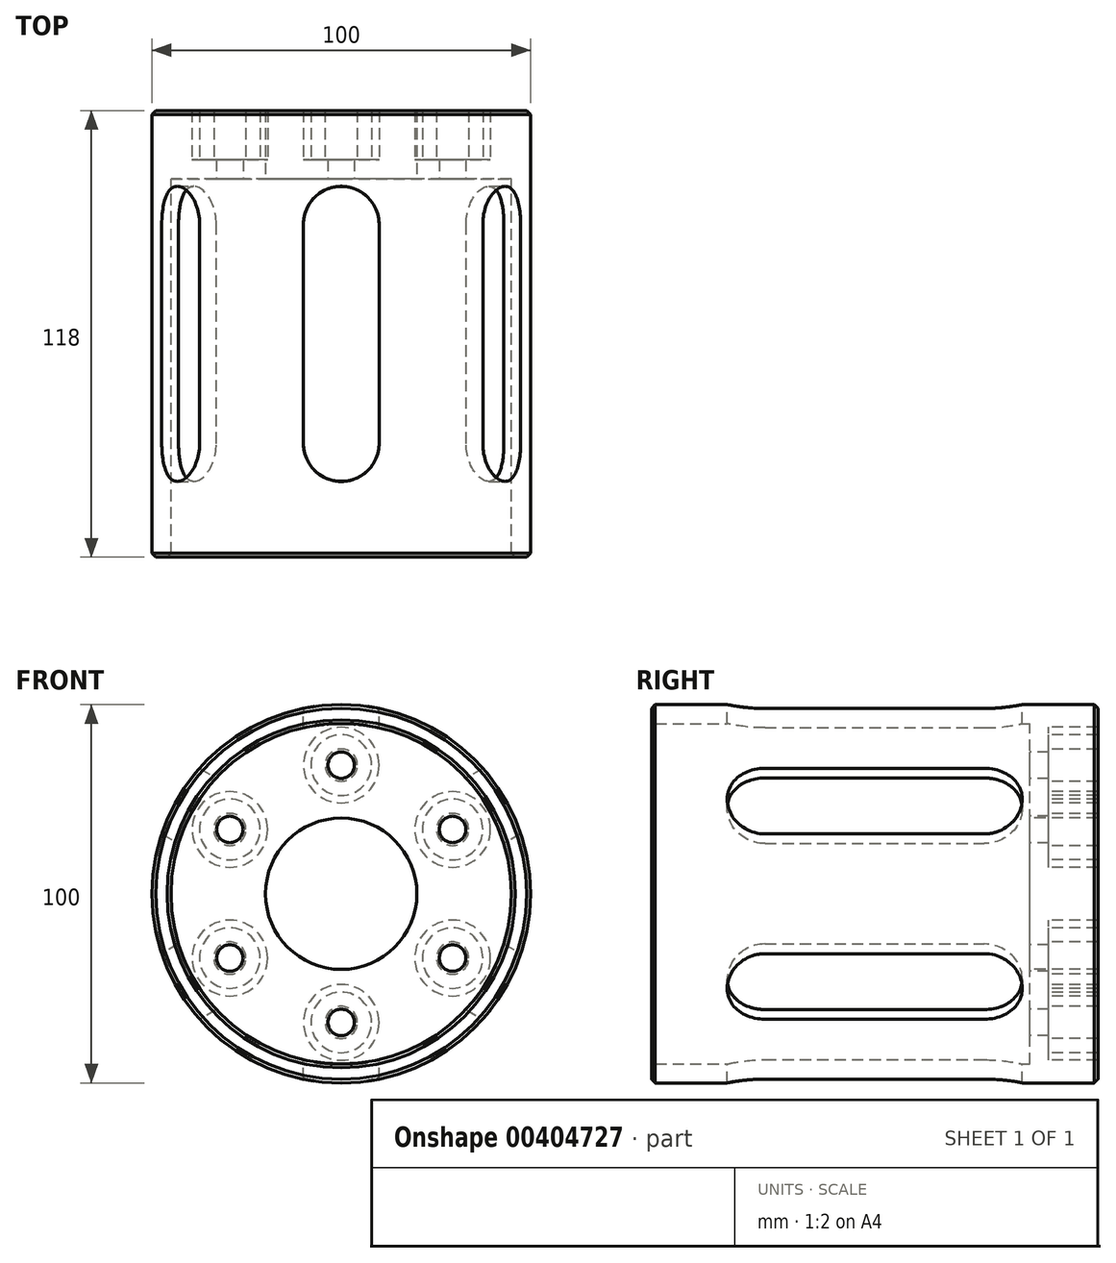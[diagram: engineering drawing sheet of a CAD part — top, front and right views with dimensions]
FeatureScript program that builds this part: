
annotation { "Feature Type Name" : "Feature", "Feature Type Description" : "" }
export const myFeature = defineFeature(function(context is Context, id is Id, definition is map)
    precondition{}
    {
        {
            var Q0;
            Q0=qCreatedBy(makeId("Top.planeOp"),FACE);
            var sketch = newSketch(context, id + "F0", { "sketchPlane" : qUnion([Q0])});
            skLineSegment(sketch, "E0", {"start": v(0, 60.4) * mm, "end": v(0, -60.4) * mm, "construction": true});
            skSolve(sketch);
        }
        {
            var Q0;
            Q0=qCreatedBy(makeId("Front.planeOp"),FACE);
            var sketch = newSketch(context, id + "F1", { "sketchPlane" : qUnion([Q0])});
            skCircle(sketch, "E1", {"center": v(0, 0) * mm, "radius": 50 * mm});
            skCircle(sketch, "E2", {"center": v(0, 34) * mm, "radius": 10 * mm});
            skCircle(sketch, "E3", {"center": v(0, 34) * mm, "radius": 4.25 * mm});
            skCircle(sketch, "E4", {"center": v(0, 34) * mm, "radius": 8 * mm});
            skCircle(sketch, "E5", {"center": v(0, 0) * mm, "radius": 20 * mm});
            skCircle(sketch, "E6", {"center": v(0, 0) * mm, "radius": 45 * mm});
            skCircle(sketch, "E7", {"center": v(0, 34) * mm, "radius": 3.5 * mm});
            skCircle(sketch, "E8.1.0", {"center": v(-29.44, 17) * mm, "radius": 3.5 * mm});
            skCircle(sketch, "E8.1.1", {"center": v(-29.44, 17) * mm, "radius": 4.25 * mm});
            skCircle(sketch, "E8.1.2", {"center": v(-29.44, 17) * mm, "radius": 10 * mm});
            skCircle(sketch, "E8.1.3", {"center": v(-29.44, 17) * mm, "radius": 8 * mm});
            skCircle(sketch, "E8.2.0", {"center": v(-29.44, -17) * mm, "radius": 3.5 * mm});
            skCircle(sketch, "E8.2.1", {"center": v(-29.44, -17) * mm, "radius": 4.25 * mm});
            skCircle(sketch, "E8.2.2", {"center": v(-29.44, -17) * mm, "radius": 10 * mm});
            skCircle(sketch, "E8.2.3", {"center": v(-29.44, -17) * mm, "radius": 8 * mm});
            skCircle(sketch, "E8.3.0", {"center": v(0, -34) * mm, "radius": 3.5 * mm});
            skCircle(sketch, "E8.3.1", {"center": v(0, -34) * mm, "radius": 4.25 * mm});
            skCircle(sketch, "E8.3.2", {"center": v(0, -34) * mm, "radius": 10 * mm});
            skCircle(sketch, "E8.3.3", {"center": v(0, -34) * mm, "radius": 8 * mm});
            skCircle(sketch, "E8.4.0", {"center": v(29.44, -17) * mm, "radius": 3.5 * mm});
            skCircle(sketch, "E8.4.1", {"center": v(29.44, -17) * mm, "radius": 4.25 * mm});
            skCircle(sketch, "E8.4.2", {"center": v(29.44, -17) * mm, "radius": 10 * mm});
            skCircle(sketch, "E8.4.3", {"center": v(29.44, -17) * mm, "radius": 8 * mm});
            skCircle(sketch, "E8.5.0", {"center": v(29.44, 17) * mm, "radius": 3.5 * mm});
            skCircle(sketch, "E8.5.1", {"center": v(29.44, 17) * mm, "radius": 4.25 * mm});
            skCircle(sketch, "E8.5.2", {"center": v(29.44, 17) * mm, "radius": 10 * mm});
            skCircle(sketch, "E8.5.3", {"center": v(29.44, 17) * mm, "radius": 8 * mm});
            skSolve(sketch);
        }
        {
            var Q0;
            Q0=makeQuery(id+"F1.imprint","IMPRINT",FACE,{"disambiguationData":[TD([[makeQuery(id+"F1.imprint","IMPRINT",EDGE,{"derivedFrom":sQuery(id+"F1.wireOp",EDGE,"E2")}),-1.0]])]});
            var Q1;
            Q1=makeQuery(id+"F1.imprint","IMPRINT",FACE,{"disambiguationData":[TD([[makeQuery(id+"F1.imprint","IMPRINT",EDGE,{"derivedFrom":sQuery(id+"F1.wireOp",EDGE,"E8.1.1")}),-1.0]])]});
            var Q2;
            Q2=makeQuery(id+"F1.imprint","IMPRINT",FACE,{"disambiguationData":[TD([[makeQuery(id+"F1.imprint","IMPRINT",EDGE,{"derivedFrom":sQuery(id+"F1.wireOp",EDGE,"E3")}),-1.0]])]});
            var Q3;
            Q3=makeQuery(id+"F1.imprint","IMPRINT",FACE,{"disambiguationData":[TD([[makeQuery(id+"F1.imprint","IMPRINT",EDGE,{"derivedFrom":sQuery(id+"F1.wireOp",EDGE,"E8.5.1")}),-1.0]])]});
            var Q4;
            Q4=makeQuery(id+"F1.imprint","IMPRINT",FACE,{"disambiguationData":[TD([[makeQuery(id+"F1.imprint","IMPRINT",EDGE,{"derivedFrom":sQuery(id+"F1.wireOp",EDGE,"E8.2.1")}),-1.0]])]});
            var Q5;
            Q5=makeQuery(id+"F1.imprint","IMPRINT",FACE,{"disambiguationData":[TD([[makeQuery(id+"F1.imprint","IMPRINT",EDGE,{"derivedFrom":sQuery(id+"F1.wireOp",EDGE,"E8.3.1")}),-1.0]])]});
            var Q6;
            Q6=makeQuery(id+"F1.imprint","IMPRINT",FACE,{"disambiguationData":[TD([[makeQuery(id+"F1.imprint","IMPRINT",EDGE,{"derivedFrom":sQuery(id+"F1.wireOp",EDGE,"E8.4.1")}),-1.0]])]});
            var Q7;
            Q7=makeQuery(id+"F1.imprint","IMPRINT",FACE,{"disambiguationData":[TD([[makeQuery(id+"F1.imprint","IMPRINT",EDGE,{"derivedFrom":sQuery(id+"F1.wireOp",EDGE,"E1")}),1.0]])]});
            extrude(context, id + "F2", {"entities" : qUnion([Q0, Q1, Q2, Q3, Q4, Q5, Q6, Q7]), "oppositeDirection" : true, "depth" : 18 * mm});
        }
        {
            var Q0;
            Q0=makeQuery(id+"F1.imprint","IMPRINT",FACE,{"disambiguationData":[TD([[makeQuery(id+"F1.imprint","IMPRINT",EDGE,{"derivedFrom":sQuery(id+"F1.wireOp",EDGE,"E2")}),1.0]])]});
            var Q1;
            Q1=makeQuery(id+"F1.imprint","IMPRINT",FACE,{"disambiguationData":[TD([[makeQuery(id+"F1.imprint","IMPRINT",EDGE,{"derivedFrom":sQuery(id+"F1.wireOp",EDGE,"E8.1.2")}),1.0]])]});
            var Q2;
            Q2=makeQuery(id+"F1.imprint","IMPRINT",FACE,{"disambiguationData":[TD([[makeQuery(id+"F1.imprint","IMPRINT",EDGE,{"derivedFrom":sQuery(id+"F1.wireOp",EDGE,"E8.2.2")}),1.0]])]});
            var Q3;
            Q3=makeQuery(id+"F1.imprint","IMPRINT",FACE,{"disambiguationData":[TD([[makeQuery(id+"F1.imprint","IMPRINT",EDGE,{"derivedFrom":sQuery(id+"F1.wireOp",EDGE,"E8.3.2")}),1.0]])]});
            var Q4;
            Q4=makeQuery(id+"F1.imprint","IMPRINT",FACE,{"disambiguationData":[TD([[makeQuery(id+"F1.imprint","IMPRINT",EDGE,{"derivedFrom":sQuery(id+"F1.wireOp",EDGE,"E8.4.2")}),1.0]])]});
            var Q5;
            Q5=makeQuery(id+"F1.imprint","IMPRINT",FACE,{"disambiguationData":[TD([[makeQuery(id+"F1.imprint","IMPRINT",EDGE,{"derivedFrom":sQuery(id+"F1.wireOp",EDGE,"E8.5.2")}),1.0]])]});
            var Q6;
            Q6=makeQuery(id+"F1.imprint","IMPRINT",FACE,{"disambiguationData":[TD([[makeQuery(id+"F1.imprint","IMPRINT",EDGE,{"derivedFrom":sQuery(id+"F1.wireOp",EDGE,"E8.1.0")}),-1.0]])]});
            var Q7;
            Q7=makeQuery(id+"F1.imprint","IMPRINT",FACE,{"disambiguationData":[TD([[makeQuery(id+"F1.imprint","IMPRINT",EDGE,{"derivedFrom":sQuery(id+"F1.wireOp",EDGE,"E3")}),1.0]])]});
            var Q8;
            Q8=makeQuery(id+"F1.imprint","IMPRINT",FACE,{"disambiguationData":[TD([[makeQuery(id+"F1.imprint","IMPRINT",EDGE,{"derivedFrom":sQuery(id+"F1.wireOp",EDGE,"E8.5.0")}),-1.0]])]});
            var Q9;
            Q9=makeQuery(id+"F1.imprint","IMPRINT",FACE,{"disambiguationData":[TD([[makeQuery(id+"F1.imprint","IMPRINT",EDGE,{"derivedFrom":sQuery(id+"F1.wireOp",EDGE,"E8.2.0")}),-1.0]])]});
            var Q10;
            Q10=makeQuery(id+"F1.imprint","IMPRINT",FACE,{"disambiguationData":[TD([[makeQuery(id+"F1.imprint","IMPRINT",EDGE,{"derivedFrom":sQuery(id+"F1.wireOp",EDGE,"E8.3.0")}),-1.0]])]});
            var Q11;
            Q11=makeQuery(id+"F1.imprint","IMPRINT",FACE,{"disambiguationData":[TD([[makeQuery(id+"F1.imprint","IMPRINT",EDGE,{"derivedFrom":sQuery(id+"F1.wireOp",EDGE,"E8.4.0")}),-1.0]])]});
            extrude(context, id + "F3", {"entities" : qUnion([Q0, Q1, Q2, Q3, Q4, Q5, Q6, Q7, Q8, Q9, Q10, Q11]), "operationType" : NewBodyOperationType.ADD, "oppositeDirection" : true, "depth" : 5 * mm});
        }
        {
            var Q0;
            Q0=makeQuery(id+"F1.imprint","IMPRINT",FACE,{"disambiguationData":[TD([[makeQuery(id+"F1.imprint","IMPRINT",EDGE,{"derivedFrom":sQuery(id+"F1.wireOp",EDGE,"E1")}),1.0]])]});
            extrude(context, id + "F4", {"entities" : qUnion([Q0]), "operationType" : NewBodyOperationType.ADD, "depth" : 100 * mm});
        }
        {
            var Q0;
            Q0=qCreatedBy(makeId("Top.planeOp"),FACE);
            var sketch = newSketch(context, id + "F5", { "sketchPlane" : qUnion([Q0])});
            skArc(sketch, "E9", {"start": v(10, -12) * mm, "mid": v(0, -2) * mm, "end": v(-10, -12) * mm});
            skArc(sketch, "E10", {"start": v(-10, -70) * mm, "mid": v(0, -80) * mm, "end": v(10, -70) * mm});
            skLineSegment(sketch, "E11", {"start": v(-10, -12) * mm, "end": v(-10, -70) * mm});
            skLineSegment(sketch, "E12", {"start": v(10, -12) * mm, "end": v(10, -70) * mm});
            skSolve(sketch);
        }
        {
            var Q0;
            Q0 = qSketchRegion(id + "F5", true);
            extrude(context, id + "F6", {"entities" : qUnion([Q0]), "operationType" : NewBodyOperationType.REMOVE, "endBound" : BoundingType.THROUGH_ALL, "oppositeDirection" : true, "depth" : 25 * mm, "hasSecondDirection" : true, "secondDirectionBound" : BoundingType.THROUGH_ALL, "secondDirectionOppositeDirection" : false, "secondDirectionDepth" : 25 * mm});
        }
        {
            var Q0;
            Q0=sQuery(id+"F0.wireOp",EDGE,"E0");
            var Q1;
            Q1=qCreatedBy(makeId("Top.planeOp"),FACE);
            cPlane(context, id + "F7", {"entities" : qUnion([Q0, Q1]), "cplaneType" : CPlaneType.LINE_ANGLE, "offset" : 25 * mm, "angle" : 60 * degree, "width" : 150 * mm, "height" : 150 * mm});
        }
        {
            var Q0;
            Q0=qCreatedBy(id+"F7.planeOp",FACE);
            var sketch = newSketch(context, id + "F8", { "sketchPlane" : qUnion([Q0])});
            skLineSegment(sketch, "E13", {"start": v(-12, -10) * mm, "end": v(-70, -10) * mm});
            skLineSegment(sketch, "E14", {"start": v(-70, 10) * mm, "end": v(-12, 10) * mm});
            skArc(sketch, "E15", {"start": v(-12, -10) * mm, "mid": v(-2, 0) * mm, "end": v(-12, 10) * mm});
            skArc(sketch, "E16", {"start": v(-70, -10) * mm, "mid": v(-80, 0) * mm, "end": v(-70, 10) * mm});
            skSolve(sketch);
        }
        {
            var Q0;
            Q0 = qSketchRegion(id + "F8", true);
            extrude(context, id + "F9", {"entities" : qUnion([Q0]), "operationType" : NewBodyOperationType.REMOVE, "endBound" : BoundingType.THROUGH_ALL, "oppositeDirection" : true, "depth" : 25 * mm, "hasSecondDirection" : true, "secondDirectionBound" : BoundingType.THROUGH_ALL, "secondDirectionOppositeDirection" : false, "secondDirectionDepth" : 25 * mm});
        }
        {
            var Q0;
            Q0=qCreatedBy(makeId("Top.planeOp"),FACE);
            var Q1;
            Q1=sQuery(id+"F0.wireOp",EDGE,"E0");
            cPlane(context, id + "F10", {"entities" : qUnion([Q0, Q1]), "cplaneType" : CPlaneType.LINE_ANGLE, "offset" : 25 * mm, "angle" : 300 * degree, "width" : 150 * mm, "height" : 150 * mm});
        }
        {
            var Q0;
            Q0=qCreatedBy(id+"F10.planeOp",FACE);
            var sketch = newSketch(context, id + "F11", { "sketchPlane" : qUnion([Q0])});
            skLineSegment(sketch, "E17.bottom", {"start": v(12, 10) * mm, "end": v(70, 10) * mm});
            skLineSegment(sketch, "E17.top", {"start": v(12, -10) * mm, "end": v(70, -10) * mm});
            skArc(sketch, "E18", {"start": v(70, 10) * mm, "mid": v(80, 0) * mm, "end": v(70, -10) * mm});
            skArc(sketch, "E19", {"start": v(12, -10) * mm, "mid": v(2, 0) * mm, "end": v(12, 10) * mm});
            skSolve(sketch);
        }
        {
            var Q0;
            Q0 = qSketchRegion(id + "F11", true);
            extrude(context, id + "F12", {"entities" : qUnion([Q0]), "operationType" : NewBodyOperationType.REMOVE, "endBound" : BoundingType.THROUGH_ALL, "oppositeDirection" : true, "depth" : 25 * mm, "hasSecondDirection" : true, "secondDirectionBound" : BoundingType.THROUGH_ALL, "secondDirectionOppositeDirection" : false, "secondDirectionDepth" : 25 * mm});
        }
        {
            var Q0;
            Q0=makeQuery(id+"F4.opExtrude","CAP_EDGE",EDGE,{"disambiguationData":[OSD([sQuery(id+"F1.wireOp",EDGE,"E6")])],"isStart":false});
            var Q1;
            Q1=makeQuery(id+"F4.opExtrude","CAP_EDGE",EDGE,{"disambiguationData":[OSD([sQuery(id+"F1.wireOp",EDGE,"E1")])],"isStart":false});
            var Q2;
            Q2=makeQuery(id+"F2.opExtrude","CAP_EDGE",EDGE,{"disambiguationData":[OSD([sQuery(id+"F1.wireOp",EDGE,"E1")])],"isStart":false});
            chamfer(context, id + "F13", {"entities" : qUnion([Q0, Q1, Q2]), "width" : 1 * mm, "tangentPropagation" : true});
        }
    });
